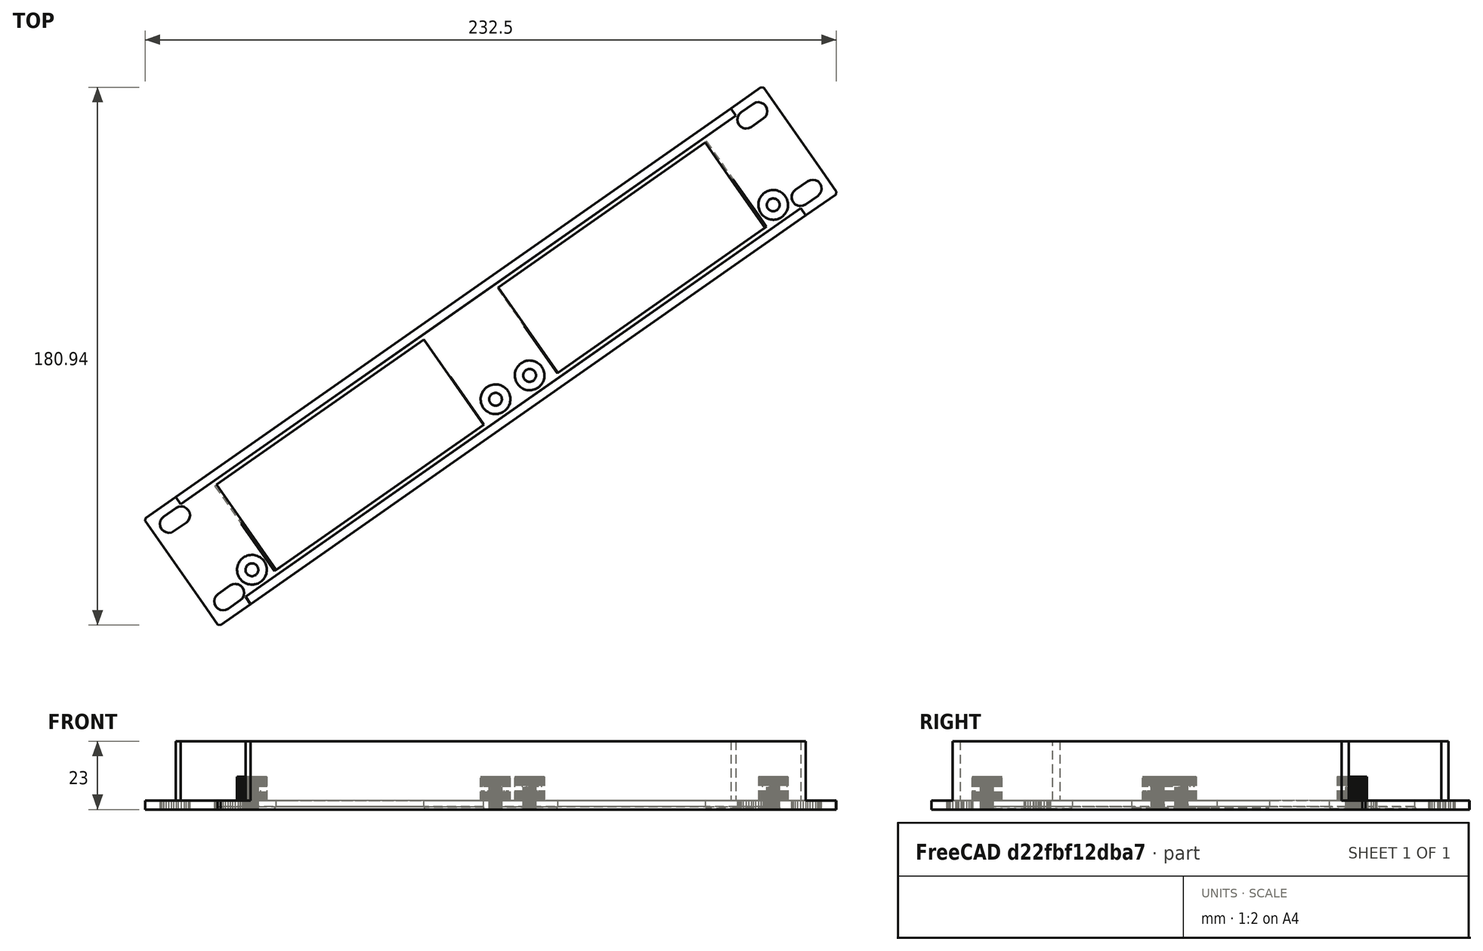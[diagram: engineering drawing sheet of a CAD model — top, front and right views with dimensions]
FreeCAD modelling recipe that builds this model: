
FCSTD DOCUMENT  (FreeCAD 0.21R33771 (Git))
Label: rack
License: All rights reserved
LicenseURL: https://en.wikipedia.org/wiki/All_rights_reserved
objects: Part::Feature×2, Mesh::Feature×1, PartDesign::FeatureBase×1, Sketcher::SketchObject×1, PartDesign::Pocket×1, PartDesign::Body×1
note: 7 computed .brp shape members not serialized (recipe doc carries the construction recipe); baked Part::Feature solids carry a one-line shape summary decoded from their .brp

FEATURE [Mesh::Feature] _0in_Rack_Double_RaspberryPi4B_exported  label="10in-Rack-Double-RaspberryPi4B_exported"
FEATURE [Part::Feature] _0in_Rack_Double_RaspberryPi4B_exported001
  shape: bbox 232.5 x 180.9 x 23 mm, 3888 faces, 0 solids (baked)
FEATURE [Part::Feature] _0in_Rack_Double_RaspberryPi4B_exported001_solid  label="_0in_Rack_Double_RaspberryPi4B_exported001 (Solid)"
  shape: bbox 232.5 x 180.9 x 23 mm, 3888 faces (baked)
FEATURE [PartDesign::FeatureBase] BaseFeature
  BaseFeature = -> _0in_Rack_Double_RaspberryPi4B_exported001_solid
FEATURE [Sketcher::SketchObject] Sketch
  ExternalGeometry = -> [BaseFeature]
  FullyConstrained = false
  MapMode = 5
  Placement = pos=(0,0,3) rot=(0,0,1;0rad)
  Support = -> [BaseFeature]
  sketch-geometry (4):
    g0: LineSegment StartX=198.973 StartY=190.875 StartZ=0 EndX=231.608 EndY=144.267 EndZ=0
    g1: LineSegment StartX=231.608 StartY=144.267 StartZ=0 EndX=253.852 EndY=159.843 EndZ=0
    g2: LineSegment StartX=253.852 StartY=159.843 StartZ=0 EndX=221.217 EndY=206.45 EndZ=0
    g3: LineSegment StartX=221.217 StartY=206.45 StartZ=0 EndX=198.973 EndY=190.875 EndZ=0
  constraints (8):
    c: Coincident(g0,g1)
    c: Coincident(g1,g2)
    c: Coincident(g2,g3)
    c: Coincident(g3,g0)
    c: Perpendicular(g0,g3)
    c: Perpendicular(g2,g3)
    c: Perpendicular(g1,g2)
    c: Parallel(g2,g-3)
FEATURE [PartDesign::Pocket] Pocket
  BaseFeature = -> BaseFeature
  Direction = (0,0,-1)
  Length = 5
  Length2 = 5
  Profile = -> Sketch
  ReferenceAxis = -> Sketch [N_Axis]
  Reversed = true
  Type = 0
FEATURE [PartDesign::Body] Body
  BaseFeature = -> _0in_Rack_Double_RaspberryPi4B_exported001_solid
  Group = -> [BaseFeature,Sketch,Pocket]
  Origin = -> Origin
  Tip = -> Pocket
